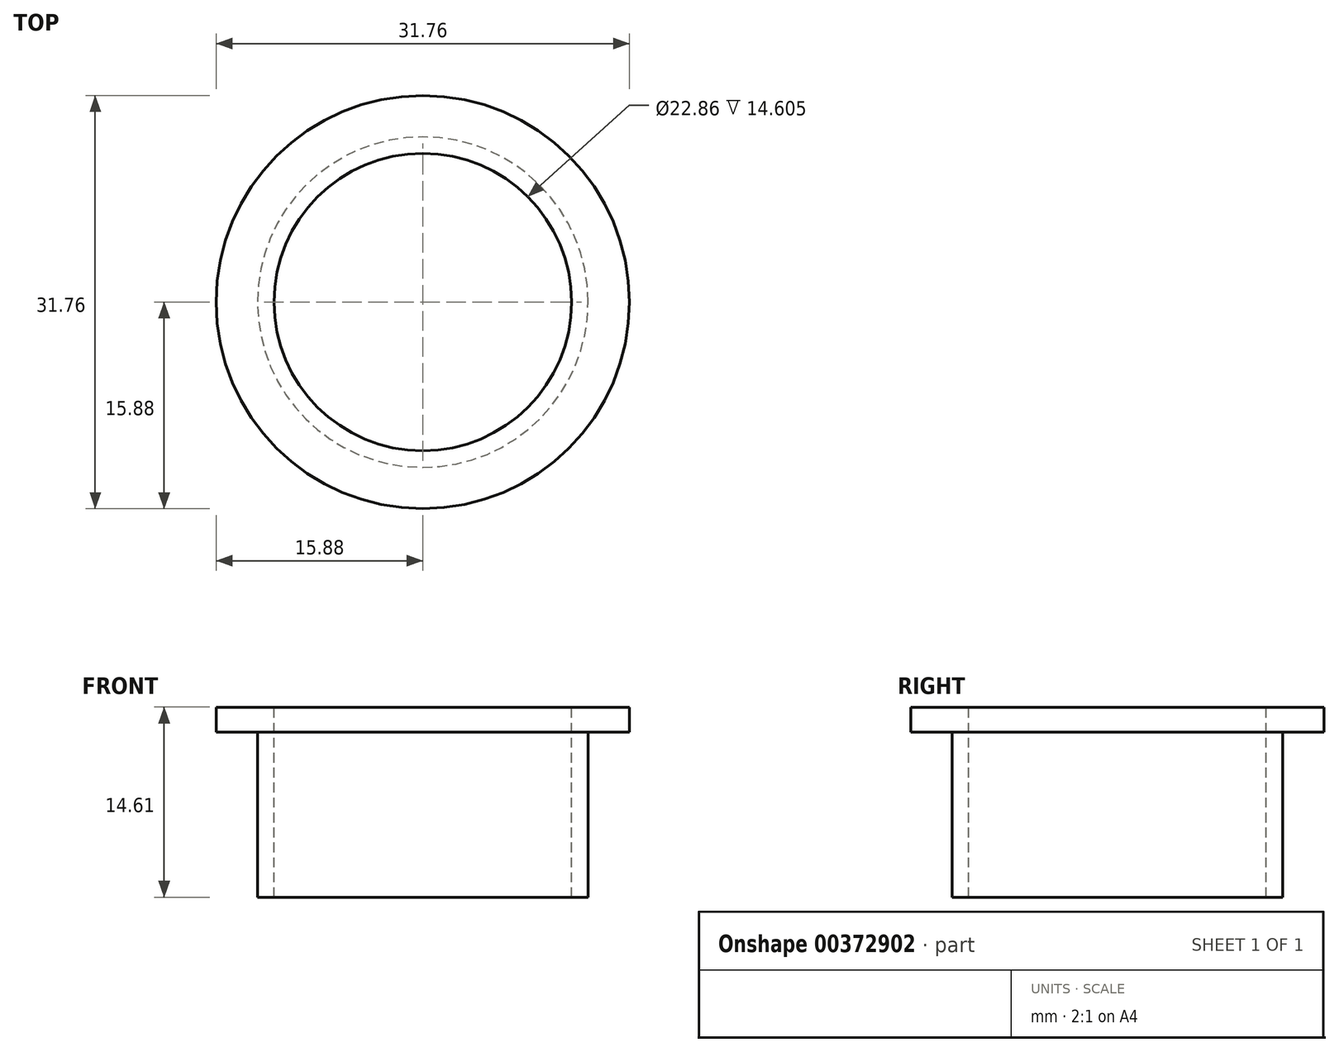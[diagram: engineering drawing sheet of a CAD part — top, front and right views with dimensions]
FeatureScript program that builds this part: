
annotation { "Feature Type Name" : "Feature", "Feature Type Description" : "" }
export const myFeature = defineFeature(function(context is Context, id is Id, definition is map)
    precondition{}
    {
        {
            var Q0;
            Q0=qCreatedBy(makeId("Top.planeOp"),FACE);
            var sketch = newSketch(context, id + "F0", { "sketchPlane" : qUnion([Q0])});
            skCircle(sketch, "E0", {"center": v(0, 0) * mm, "radius": 12.7 * mm});
            skSolve(sketch);
        }
        {
            var Q0;
            Q0=makeQuery(id+"F0.imprint","IMPRINT",FACE,{"disambiguationData":[TD([[makeQuery(id+"F0.imprint","IMPRINT",EDGE,{"derivedFrom":sQuery(id+"F0.wireOp",EDGE,"E0")}),1.0]])]});
            extrude(context, id + "F1", {"entities" : qUnion([Q0]), "depth" : 12.7 * mm});
        }
        {
            var Q0;
            Q0=makeQuery(id+"F1.opExtrude","CAP_FACE",FACE,{"disambiguationData":[OSD([sQuery(id+"F0.wireOp",EDGE,"E0")])],"isStart":false});
            var sketch = newSketch(context, id + "F2", { "sketchPlane" : qUnion([Q0])});
            skPoint(sketch, "E1", {"position": v(0, 0) * mm});
            skSolve(sketch);
        }
        {
            var Q0;
            Q0=sQuery(id+"F2.wireOp",VERTEX,"E1");
            var Q1;
            Q1=makeQuery(id+"F1.opExtrude","SWEPT_BODY",BODY,{"disambiguationData":[OSD([sQuery(id+"F0.wireOp",EDGE,"E0")])]});
            hole(context, id + "F3", {"style" : HoleStyle.SIMPLE, "endStyle" : HoleEndStyle.THROUGH, "holeDiameter" : 22.86 * mm, "isTappedThrough" : true, "tappedDepth" : 12.7 * mm, "tapClearance" : 3, "locations" : qUnion([Q0]), "scope" : qUnion([Q1])});
        }
        {
            var Q0;
            Q0=makeQuery(id+"F1.opExtrude","CAP_FACE",FACE,{"disambiguationData":[OSD([sQuery(id+"F0.wireOp",EDGE,"E0")])],"isStart":false});
            var sketch = newSketch(context, id + "F4", { "sketchPlane" : qUnion([Q0])});
            skCircle(sketch, "E2", {"center": v(0, 0) * mm, "radius": 15.88 * mm});
            skSolve(sketch);
        }
        {
            var Q0;
            Q0 = qSketchRegion(id + "F4", true);
            extrude(context, id + "F5", {"entities" : qUnion([Q0]), "operationType" : NewBodyOperationType.ADD, "depth" : 1.9 * mm});
        }
        {
            var Q0;
            Q0=makeQuery(id+"F5.opExtrude","CAP_FACE",FACE,{"disambiguationData":[OSD([sQuery(id+"F4.wireOp",EDGE,"E2")])],"isStart":false});
            var sketch = newSketch(context, id + "F6", { "sketchPlane" : qUnion([Q0])});
            skPoint(sketch, "E3", {"position": v(0, 0) * mm});
            skSolve(sketch);
        }
        {
            var Q0;
            Q0=sQuery(id+"F6.wireOp",VERTEX,"E3");
            var Q1;
            Q1=makeQuery(id+"F1.opExtrude","SWEPT_BODY",BODY,{"disambiguationData":[OSD([sQuery(id+"F0.wireOp",EDGE,"E0")])]});
            hole(context, id + "F7", {"style" : HoleStyle.SIMPLE, "endStyle" : HoleEndStyle.THROUGH, "holeDiameter" : 22.86 * mm, "isTappedThrough" : true, "tappedDepth" : 12.7 * mm, "tapClearance" : 3, "locations" : qUnion([Q0]), "scope" : qUnion([Q1])});
        }
    });
